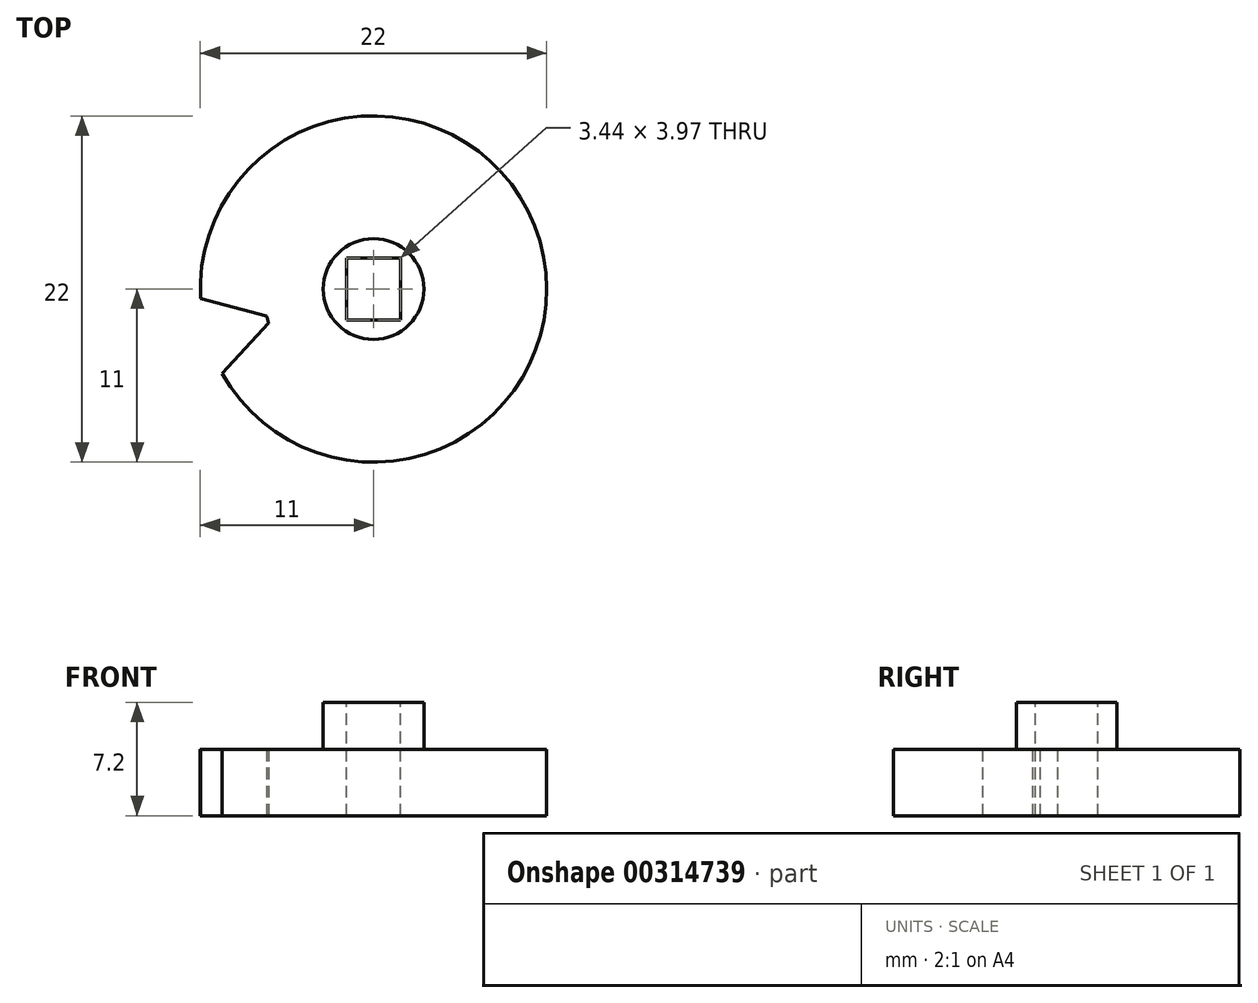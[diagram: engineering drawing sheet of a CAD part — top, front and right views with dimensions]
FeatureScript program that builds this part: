
annotation { "Feature Type Name" : "Feature", "Feature Type Description" : "" }
export const myFeature = defineFeature(function(context is Context, id is Id, definition is map)
    precondition{}
    {
        {
            var Q0;
            Q0=qCreatedBy(makeId("Top.planeOp"),FACE);
            var sketch = newSketch(context, id + "F0", { "sketchPlane" : qUnion([Q0])});
            skCircle(sketch, "E0", {"center": v(0, 0) * mm, "radius": 11 * mm});
            skSolve(sketch);
        }
        {
            var Q0;
            Q0 = qSketchRegion(id + "F0", true);
            extrude(context, id + "F1", {"entities" : qUnion([Q0]), "depth" : 4.2 * mm});
        }
        {
            var Q0;
            Q0=makeQuery(id+"F1.opExtrude","CAP_FACE",FACE,{"disambiguationData":[OSD([sQuery(id+"F0.wireOp",EDGE,"E0")])],"isStart":true});
            var sketch = newSketch(context, id + "F2", { "sketchPlane" : qUnion([Q0])});
            skLineSegment(sketch, "E1", {"start": v(0, 0) * mm, "end": v(-10.57, 3.05) * mm});
            skLineSegment(sketch, "E2", {"start": v(0, 0) * mm, "end": v(-6.79, 1.7) * mm});
            skLineSegment(sketch, "E3", {"start": v(0, 0) * mm, "end": v(-6.65, 2.18) * mm});
            skLineSegment(sketch, "E4", {"start": v(0, 0) * mm, "end": v(-10.98, 0.6) * mm});
            skLineSegment(sketch, "E5", {"start": v(0, 0) * mm, "end": v(-9.61, 5.35) * mm});
            skArc(sketch, "E6", {"start": v(-6.79, 1.7) * mm, "mid": v(-6.73, 1.94) * mm, "end": v(-6.65, 2.18) * mm});
            skLineSegment(sketch, "E7", {"start": v(-10.98, 0.6) * mm, "end": v(-0.93, 0.05) * mm});
            skLineSegment(sketch, "E8", {"start": v(-10.98, 0.6) * mm, "end": v(-6.26, 0.34) * mm});
            skLineSegment(sketch, "E9", {"start": v(-10.98, 0.6) * mm, "end": v(-6.79, 1.7) * mm});
            skArc(sketch, "E10", {"start": v(-10.98, 0.6) * mm, "mid": v(-10.57, 3.05) * mm, "end": v(-9.61, 5.35) * mm});
            skLineSegment(sketch, "E11", {"start": v(-6.65, 2.18) * mm, "end": v(-9.61, 5.35) * mm});
            skSolve(sketch);
        }
        {
            var Q0;
            {var subQ5=sQuery(id+"F2.wireOp",EDGE,"E11");Q0=makeQuery(id+"F2.imprint","IMPRINT",FACE,{"disambiguationData":[TD([[makeQuery(id+"F2.imprint","IMPRINT",EDGE,{"derivedFrom":subQ5}),1.0]])]});}
            var Q1;
            {var subQ5=sQuery(id+"F2.wireOp",EDGE,"E9");Q1=makeQuery(id+"F2.imprint","IMPRINT",FACE,{"disambiguationData":[TD([[makeQuery(id+"F2.imprint","IMPRINT",EDGE,{"derivedFrom":subQ5}),1.0]])]});}
            extrude(context, id + "F3", {"entities" : qUnion([Q0, Q1]), "operationType" : NewBodyOperationType.REMOVE, "endBound" : BoundingType.THROUGH_ALL, "oppositeDirection" : true, "depth" : 25 * mm});
        }
        {
            var Q0;
            Q0=qCreatedBy(makeId("Front.planeOp"),FACE);
            var sketch = newSketch(context, id + "F4", { "sketchPlane" : qUnion([Q0])});
            skLineSegment(sketch, "E12", {"start": v(0, 0) * mm, "end": v(0, -37.91) * mm});
            skSolve(sketch);
        }
        {
            var Q0;
            Q0=makeQuery(id+"F1.opExtrude","CAP_FACE",FACE,{"disambiguationData":[OSD([sQuery(id+"F0.wireOp",EDGE,"E0")])],"isStart":false});
            var sketch = newSketch(context, id + "F5", { "sketchPlane" : qUnion([Q0])});
            skCircle(sketch, "E13", {"center": v(0, 0) * mm, "radius": 3.2 * mm});
            skSolve(sketch);
        }
        {
            var Q0;
            Q0 = qSketchRegion(id + "F5", true);
            extrude(context, id + "F6", {"entities" : qUnion([Q0]), "operationType" : NewBodyOperationType.ADD, "depth" : 3 * mm});
        }
        {
            var Q0;
            Q0=makeQuery(id+"F6.opExtrude","CAP_FACE",FACE,{"disambiguationData":[OSD([sQuery(id+"F5.wireOp",EDGE,"E13")])],"isStart":false});
            var sketch = newSketch(context, id + "F7", { "sketchPlane" : qUnion([Q0])});
            skLineSegment(sketch, "E14.bottom", {"start": v(-1.72, -1.98) * mm, "end": v(1.72, -1.98) * mm});
            skLineSegment(sketch, "E14.top", {"start": v(-1.72, 1.98) * mm, "end": v(1.72, 1.98) * mm});
            skLineSegment(sketch, "E14.left", {"start": v(-1.72, -1.98) * mm, "end": v(-1.72, 1.98) * mm});
            skLineSegment(sketch, "E14.right", {"start": v(1.72, -1.98) * mm, "end": v(1.72, 1.98) * mm});
            skPoint(sketch, "E14.middle", {"position": v(0, 0) * mm});
            skSolve(sketch);
        }
        {
            var Q0;
            Q0 = qSketchRegion(id + "F7", true);
            extrude(context, id + "F8", {"entities" : qUnion([Q0]), "operationType" : NewBodyOperationType.REMOVE, "endBound" : BoundingType.THROUGH_ALL, "oppositeDirection" : true, "depth" : 25 * mm});
        }
    });
